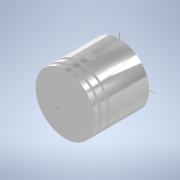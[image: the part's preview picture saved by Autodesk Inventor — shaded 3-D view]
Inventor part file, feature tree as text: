
AUTODESK INVENTOR PART (.ipt)
format: ipt  version: 2021.1 (Build 251245000, 245)  size: 214,016 bytes
history: native  units: in
note: dims shown in document units (in); Inventor stores cm internally (conversion verified against a paired STEP export)
features: projected_geometry x9, sketch x4, extrude x2, revolve x2
ambient origin geometry x8: Origin, YZ Plane, XZ Plane, XY Plane, X Axis, Y Axis, Z Axis, Center Point
bodies: Solid1 (feature_tree)
feature tree (17):
  extrude  "Extrusion1"  Depth=3.2in TaperAngle=0.0deg
  revolve  "Revolution1"  [1 undecoded]
  revolve  "Revolution2"  [1 undecoded]
  extrude  "Extrusion3"  Depth=1.6in
  sketch  "Sketch1"  dims[d0=3.2in d1=3.2in d2=0.0in]
  sketch  "Sketch2"  dims[d3=0.3in d4=2.1in]
  projected_geometry  "Projected Loop1"
  sketch  "Sketch4"  dims[d5=1.45in d6=1.45in]
  projected_geometry  "Projected Loop2"
  sketch  "Sketch5"  dims[d7=0.0687in d8=1.3in d9=1.0in d10=1.0in d11=1.4in d12=90.0deg d17=2.0in d18=90.0deg d19=0.5in d20=1.6in d21=0.0in d22=0.0in d23=0.15in d24=0.15in]
  projected_geometry  "Projected Loop3"
  projected_geometry  "Projected Loop4"
  projected_geometry  "Projected Loop5"
  projected_geometry  "Project Cut Edges1"
  projected_geometry  "Project Cut Edges2"
  projected_geometry  "Project Cut Edges4"
  projected_geometry  "Project Cut Edges5"
note: 2 required parameter values undecoded (feature->parameter linkage not recoverable at this tier; creation-order binding heuristic only, values carry confidence <= 0.55)
